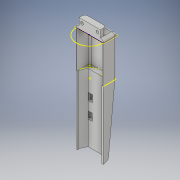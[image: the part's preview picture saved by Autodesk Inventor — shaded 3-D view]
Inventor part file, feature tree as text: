
AUTODESK INVENTOR PART (.ipt)
format: ipt  version: 2019 (Build 230136000, 136)  size: 420,864 bytes
history: native  units: in
note: dims shown in document units (in); Inventor stores cm internally (conversion verified against a paired STEP export)
features: reference x20, sketch x14, extrude x10, projected_geometry x5, other x5, plane x3, fillet x1, loft x1
ambient origin geometry x8: Origin, YZ Plane, XZ Plane, XY Plane, X Axis, Y Axis, Z Axis, Center Point
bodies: Solid1 (feature_tree)
feature tree (59):
  sketch  "Sketch1"  dims[d1=2.0in d2=0.0in d3=1.0in d4=0.0in]
  plane  "Work Plane1"
  extrude  "Extrusion1"  Depth=1.0in TaperAngle=0.0deg
  sketch  "Sketch2"  dims[d5=0.125in d6=0.0in d7=0.125in d8=0.0in]
  plane  "Work Plane2"
  extrude  "Extrusion2"  Depth=0.125in TaperAngle=0.0deg
  extrude  "Extrusion3"  Depth=0.45in
  sketch  "Sketch4"  dims[d11=0.25in d12=0.125in]
  extrude  "Extrusion4"  Depth=0.125in
  extrude  "Extrusion5"  Depth=0.125in
  extrude  "Extrusion6"  Depth=0.3in TaperAngle=0.0deg
  sketch  "Sketch9"  dims[d27=0.5512in d28=1.1024in]
  plane  "Work Plane3"
  extrude  "Extrusion9"  Depth=1.6in TaperAngle=0.0deg
  extrude  "Extrusion10"  Depth=1.1024in
  extrude  "Extrusion11"  Depth=1.6in TaperAngle=0.0deg
  fillet  "Fillet1"  Radius=0.125in
  sketch  "Sketch14"
  loft  "Loft1"
  extrude  "Extrusion12"  Depth=1.0in TaperAngle=0.0deg
  sketch  "Sketch15"
  sketch  "Sketch16"
  reference  "Reference1"
  reference  "Reference2"
  reference  "Reference4"
  reference  "Reference5"
  projected_geometry  "Projected Loop1"
  sketch  "Sketch3"  dims[d9=0.45in d10=0.45in]
  projected_geometry  "Projected Loop2"
  sketch  "Sketch5"  dims[d13=0.3in d14=0.0in d15=0.125in]
  sketch  "Sketch6"  dims[d16=0.125in d17=0.3in d18=0.0in]
  sketch  "Sketch7"  dims[d23=-0.125in d24=1.6in d25=0.0in]
  projected_geometry  "Projected Loop4"
  reference  "Reference16"
  reference  "Reference17"
  reference  "Reference18"
  reference  "Reference19"
  reference  "Reference20"
  reference  "Reference21"
  reference  "Reference22"
  reference  "Reference23"
  reference  "Reference24"
  reference  "Reference25"
  reference  "Reference26"
  reference  "Reference27"
  reference  "Reference28"
  reference  "Reference29"
  reference  "Reference30"
  reference  "Reference31"
  sketch  "Sketch11"  dims[d29=0.0625in d30=1.6in d31=0.0in d32=0.125in d33=0.0in]
  projected_geometry  "Projected Loop6"
  sketch  "Sketch12"  dims[d34=0.125in d35=0.0in d36=90.0deg]
  sketch  "Sketch13"  dims[d37=0.0in d38=90.0deg d39=1.0in d40=0.0in]
  projected_geometry  "Projected Loop7"
  other  "Edges1"
  other  "Edges2"
  other  "Rocket Case.iam"
  other  "Bottom tube:1"
  other  "Rocket_Data_Logger v1:1"
